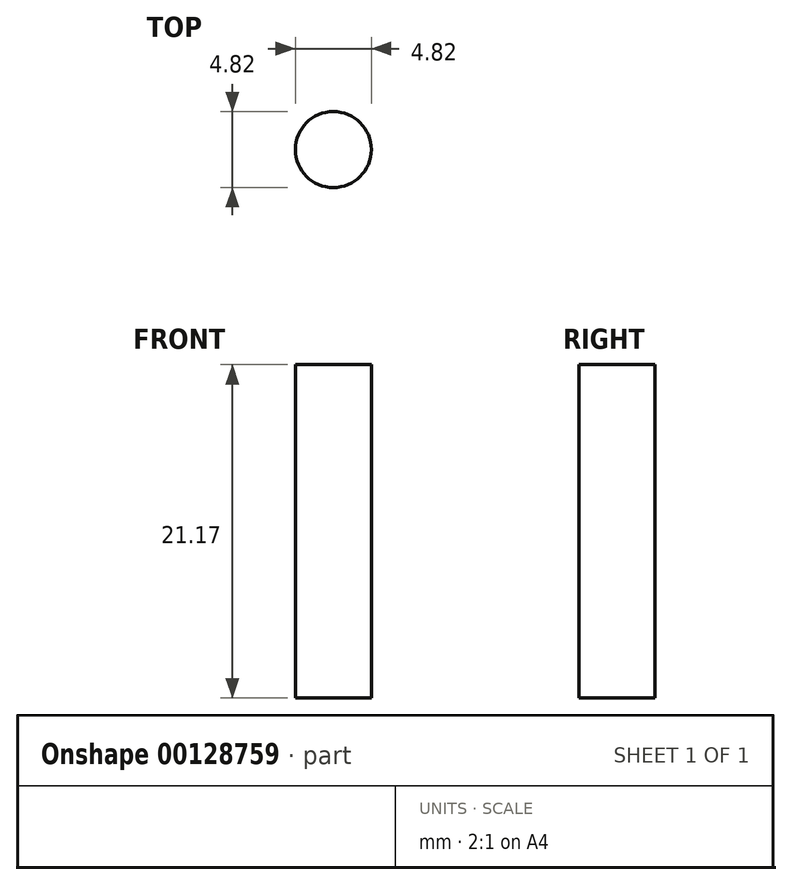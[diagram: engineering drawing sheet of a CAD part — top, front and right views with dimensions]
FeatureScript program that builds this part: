
annotation { "Feature Type Name" : "Feature", "Feature Type Description" : "" }
export const myFeature = defineFeature(function(context is Context, id is Id, definition is map)
    precondition{}
    {
        {
            var Q0;
            Q0=qCreatedBy(makeId("Top.planeOp"),FACE);
            var sketch = newSketch(context, id + "F0", { "sketchPlane" : qUnion([Q0])});
            skCircle(sketch, "E0", {"center": v(0, 0) * mm, "radius": 2.41 * mm});
            skSolve(sketch);
        }
        {
            var Q0;
            Q0 = qSketchRegion(id + "F0", true);
            extrude(context, id + "F1", {"entities" : qUnion([Q0]), "depth" : 21.17 * mm});
        }
    });
